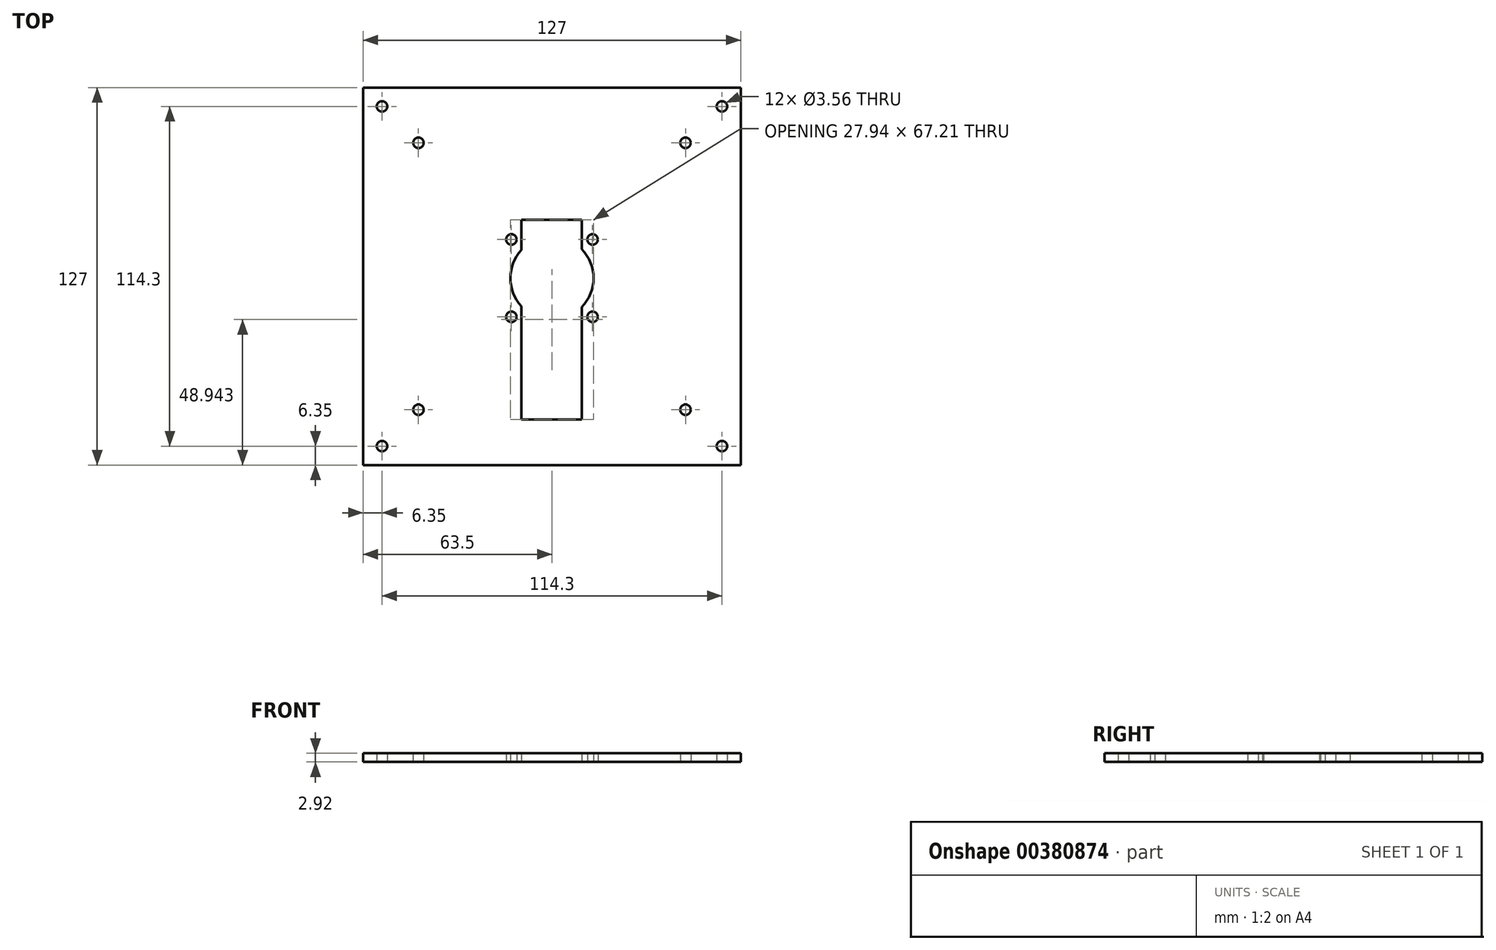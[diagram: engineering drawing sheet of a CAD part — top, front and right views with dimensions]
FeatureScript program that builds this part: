
annotation { "Feature Type Name" : "Feature", "Feature Type Description" : "" }
export const myFeature = defineFeature(function(context is Context, id is Id, definition is map)
    precondition{}
    {
        {
            var Q0;
            Q0=qCreatedBy(makeId("Top.planeOp"),FACE);
            var sketch = newSketch(context, id + "F0", { "sketchPlane" : qUnion([Q0])});
            skLineSegment(sketch, "E0.bottom", {"start": v(0, 0) * mm, "end": v(127, 0) * mm});
            skLineSegment(sketch, "E0.top", {"start": v(0, 127) * mm, "end": v(127, 127) * mm});
            skLineSegment(sketch, "E0.left", {"start": v(0, 0) * mm, "end": v(0, 127) * mm});
            skLineSegment(sketch, "E0.right", {"start": v(127, 0) * mm, "end": v(127, 127) * mm});
            skPoint(sketch, "E1", {"position": v(63.5, 63.5) * mm});
            skPoint(sketch, "E1.positionSnap0", {"position": v(0, 63.5) * mm});
            skPoint(sketch, "E1.positionSnap1", {"position": v(63.5, 127) * mm});
            skCircle(sketch, "E2", {"center": v(108.4, 108.4) * mm, "radius": 1.78 * mm});
            skCircle(sketch, "E3.1.0", {"center": v(18.6, 108.4) * mm, "radius": 1.78 * mm});
            skCircle(sketch, "E3.2.0", {"center": v(18.6, 18.6) * mm, "radius": 1.78 * mm});
            skCircle(sketch, "E3.3.0", {"center": v(108.4, 18.6) * mm, "radius": 1.78 * mm});
            skLineSegment(sketch, "E4", {"start": v(49.85, 67.95) * mm, "end": v(77.15, 67.95) * mm, "construction": true});
            skLineSegment(sketch, "E5", {"start": v(56.25, 63.5) * mm, "end": v(63.5, 63.5) * mm, "construction": true});
            skCircle(sketch, "E6.0.1.0", {"center": v(49.85, 75.88) * mm, "radius": 1.78 * mm});
            skCircle(sketch, "E6.0.1.1", {"center": v(77.15, 75.88) * mm, "radius": 1.78 * mm});
            skLineSegment(sketch, "E6.direction1", {"start": v(49.85, 67.95) * mm, "end": v(62.55, 67.95) * mm, "construction": true});
            skLineSegment(sketch, "E6.direction2", {"start": v(49.85, 67.95) * mm, "end": v(49.85, 75.88) * mm, "construction": true});
            skLineSegment(sketch, "E7", {"start": v(56.31, 62.87) * mm, "end": v(41.59, 62.87) * mm, "construction": true});
            skCircle(sketch, "E8.MirrorC", {"center": v(49.85, 49.85) * mm, "radius": 1.78 * mm});
            skCircle(sketch, "E9.MirrorC", {"center": v(77.15, 49.85) * mm, "radius": 1.78 * mm});
            skLineSegment(sketch, "E10.bottom", {"start": v(53.2, 82.55) * mm, "end": v(73.51, 82.55) * mm});
            skLineSegment(sketch, "E10.top", {"start": v(53.2, 15.34) * mm, "end": v(73.51, 15.34) * mm});
            skLineSegment(sketch, "E10.left", {"start": v(53.2, 82.55) * mm, "end": v(53.2, 72.3) * mm});
            skLineSegment(sketch, "E10.right", {"start": v(73.51, 82.55) * mm, "end": v(73.51, 72.6) * mm});
            skLineSegment(sketch, "E11", {"start": v(63.5, 63.5) * mm, "end": v(108.4, 108.4) * mm, "construction": true});
            skCircle(sketch, "E12", {"center": v(63.5, 62.87) * mm, "radius": 13.97 * mm});
            skLineSegment(sketch, "E13.trimOffspring", {"start": v(53.2, 53.44) * mm, "end": v(53.2, 15.34) * mm});
            skLineSegment(sketch, "E14.trimOffspring", {"start": v(73.51, 53.12) * mm, "end": v(73.51, 15.34) * mm});
            skCircle(sketch, "E15", {"center": v(6.35, 120.65) * mm, "radius": 1.78 * mm});
            skCircle(sketch, "E16.1.0", {"center": v(6.35, 6.35) * mm, "radius": 1.78 * mm});
            skCircle(sketch, "E16.2.0", {"center": v(120.65, 6.35) * mm, "radius": 1.78 * mm});
            skCircle(sketch, "E16.3.0", {"center": v(120.65, 120.65) * mm, "radius": 1.78 * mm});
            skSolve(sketch);
        }
        {
            var Q0;
            Q0 = qSketchRegion(id + "F0", true);
            extrude(context, id + "F1", {"entities" : qUnion([Q0]), "depth" : 2.92 * mm});
        }
    });
